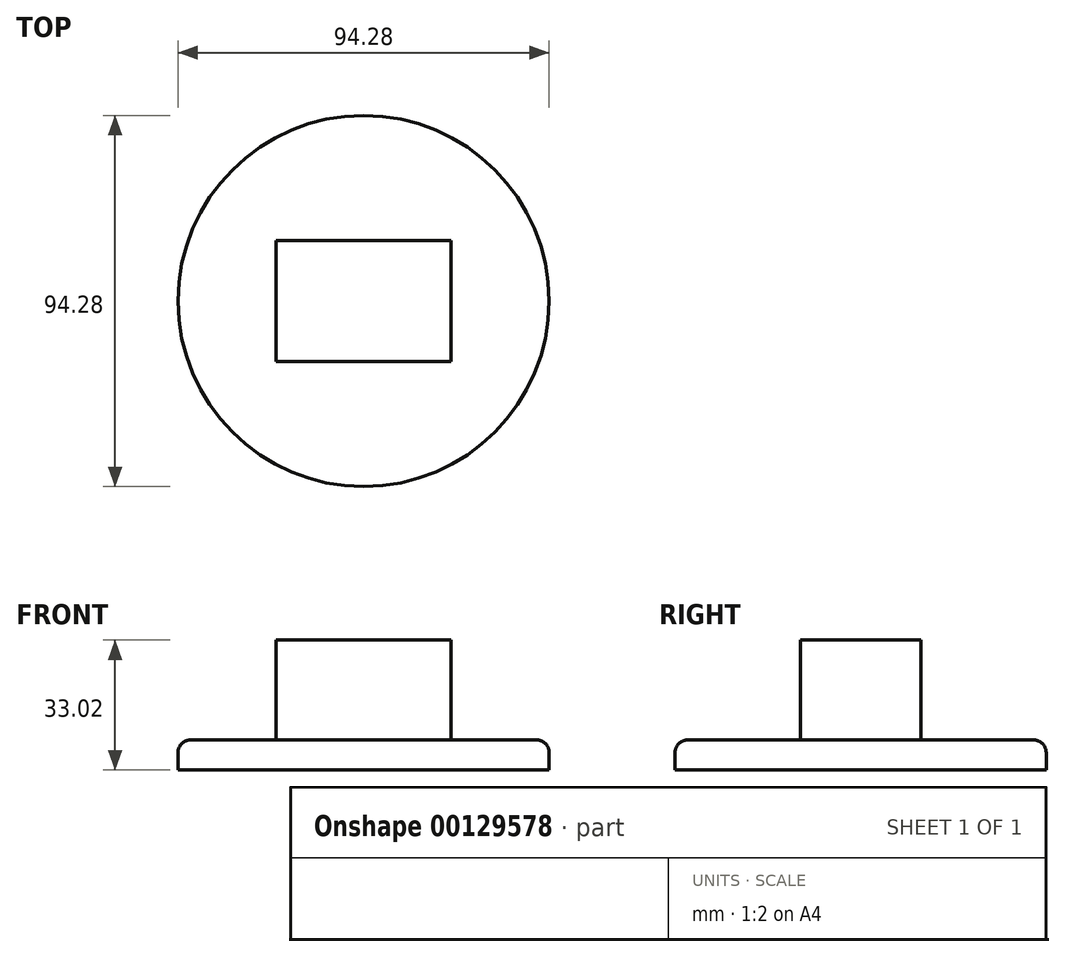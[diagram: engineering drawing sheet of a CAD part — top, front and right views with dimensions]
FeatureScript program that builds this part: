
annotation { "Feature Type Name" : "Feature", "Feature Type Description" : "" }
export const myFeature = defineFeature(function(context is Context, id is Id, definition is map)
    precondition{}
    {
        {
            var Q0;
            Q0=qCreatedBy(makeId("Top.planeOp"),FACE);
            var sketch = newSketch(context, id + "F0", { "sketchPlane" : qUnion([Q0])});
            skCircle(sketch, "E0", {"center": v(0, 0) * mm, "radius": 47.14 * mm});
            skSolve(sketch);
        }
        {
            var Q0;
            Q0 = qSketchRegion(id + "F0", true);
            var Q1;
            Q1=makeQuery(id+"F0.imprint","IMPRINT",FACE,{"disambiguationData":[TD([[makeQuery(id+"F0.imprint","IMPRINT",EDGE,{"derivedFrom":sQuery(id+"F0.wireOp",EDGE,"E0")}),1.0]])]});
            extrude(context, id + "F1", {"entities" : qUnion([Q0, Q1]), "depth" : 7.62 * mm});
        }
        {
            var Q0;
            Q0=makeQuery(id+"F1.opExtrude","CAP_EDGE",EDGE,{"disambiguationData":[OSD([sQuery(id+"F0.wireOp",EDGE,"E0")])],"isStart":false});
            fillet(context, id + "F2", {"entities" : qUnion([Q0]), "radius" : 3.15 * mm, "tangentPropagation" : true, "allowEdgeOverflow" : false});
        }
        {
            var Q0;
            Q0=makeQuery(id+"F1.opExtrude","CAP_FACE",FACE,{"disambiguationData":[OSD([sQuery(id+"F0.wireOp",EDGE,"E0")])],"isStart":false});
            var sketch = newSketch(context, id + "F3", { "sketchPlane" : qUnion([Q0])});
            skSolve(sketch);
        }
        {
            var Q0;
            {var subQ0=sQuery(id+"F0.wireOp",EDGE,"E0");Q0=makeQuery(id+"F3.imprint","IMPRINT",FACE,{"disambiguationData":[TD([[makeQuery(id+"F3.imprint","IMPRINT",EDGE,{"derivedFrom":makeQuery(id+"F2.opFillet","BLEND_EDGE",EDGE,{"blendedFrom":[makeQuery(id+"F1.opExtrude","CAP_EDGE",EDGE,{"disambiguationData":[OSD([subQ0])],"isStart":false}),makeQuery(id+"F1.opExtrude","CAP_FACE",FACE,{"disambiguationData":[OSD([subQ0])],"isStart":false})],"blendedInto":[makeQuery(id+"F1.opExtrude","CAP_FACE",FACE,{"disambiguationData":[OSD([subQ0])],"isStart":false})]})}),1.0]])]});}
            var sketch = newSketch(context, id + "F4", { "sketchPlane" : qUnion([Q0])});
            skLineSegment(sketch, "E1.bottom", {"start": v(-22.23, 15.35) * mm, "end": v(22.23, 15.35) * mm});
            skLineSegment(sketch, "E1.top", {"start": v(-22.23, -15.35) * mm, "end": v(22.23, -15.35) * mm});
            skLineSegment(sketch, "E1.left", {"start": v(-22.23, 15.35) * mm, "end": v(-22.23, -15.35) * mm});
            skLineSegment(sketch, "E1.right", {"start": v(22.23, 15.35) * mm, "end": v(22.23, -15.35) * mm});
            skPoint(sketch, "E1.middle", {"position": v(0, 0) * mm});
            skSolve(sketch);
        }
        {
            var Q0;
            Q0 = qSketchRegion(id + "F4", true);
            extrude(context, id + "F5", {"entities" : qUnion([Q0]), "operationType" : NewBodyOperationType.ADD, "depth" : 25.4 * mm});
        }
    });
